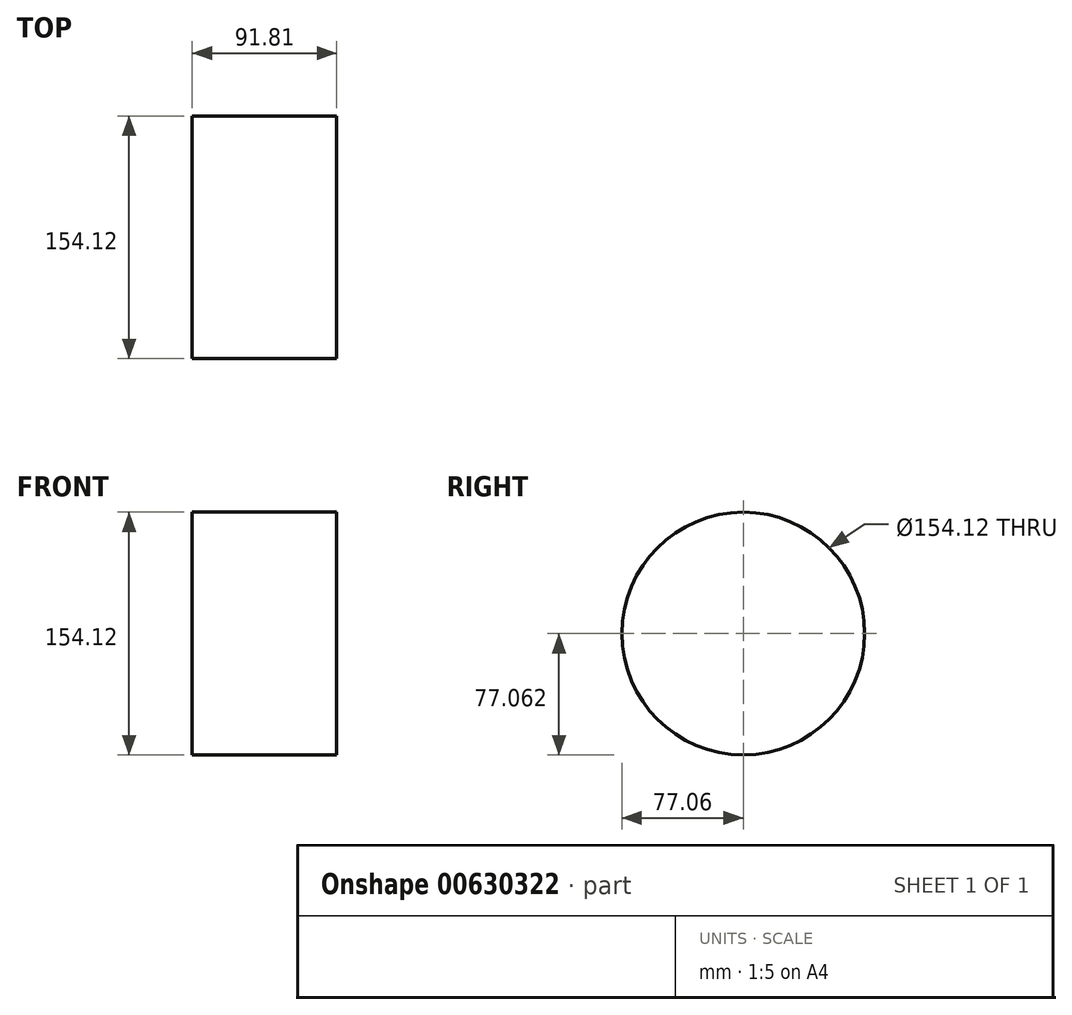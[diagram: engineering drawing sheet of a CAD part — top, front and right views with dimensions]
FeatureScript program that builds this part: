
annotation { "Feature Type Name" : "Feature", "Feature Type Description" : "" }
export const myFeature = defineFeature(function(context is Context, id is Id, definition is map)
    precondition{}
    {
        {
            var Q0;
            Q0=qCreatedBy(makeId("Front.planeOp"),FACE);
            var sketch = newSketch(context, id + "F0", { "sketchPlane" : qUnion([Q0])});
            skLineSegment(sketch, "E0.bottom", {"start": v(91.81, 77.06) * mm, "end": v(0, 77.06) * mm, "construction": true});
            skLineSegment(sketch, "E0.top", {"start": v(91.81, 0) * mm, "end": v(0, 0) * mm});
            skLineSegment(sketch, "E0.left", {"start": v(91.81, 77.06) * mm, "end": v(91.81, 0) * mm});
            skLineSegment(sketch, "E0.right", {"start": v(0, 77.06) * mm, "end": v(0, 0) * mm});
            skSolve(sketch);
        }
        {
            var Q0;
            Q0 = qSketchRegion(id + "F0", true);
            var Q1;
            Q1=sQuery(id+"F0.wireOp",EDGE,"E0.top");
            var Q2;
            Q2=sQuery(id+"F0.wireOp",EDGE,"E0.bottom");
            revolve(context, id + "F1", {"bodyType" : ToolBodyType.SURFACE, "entities" : qUnion([Q0]), "surfaceEntities" : qUnion([Q1]), "axis" : qUnion([Q2]), "revolveType" : RevolveType.FULL});
        }
    });
